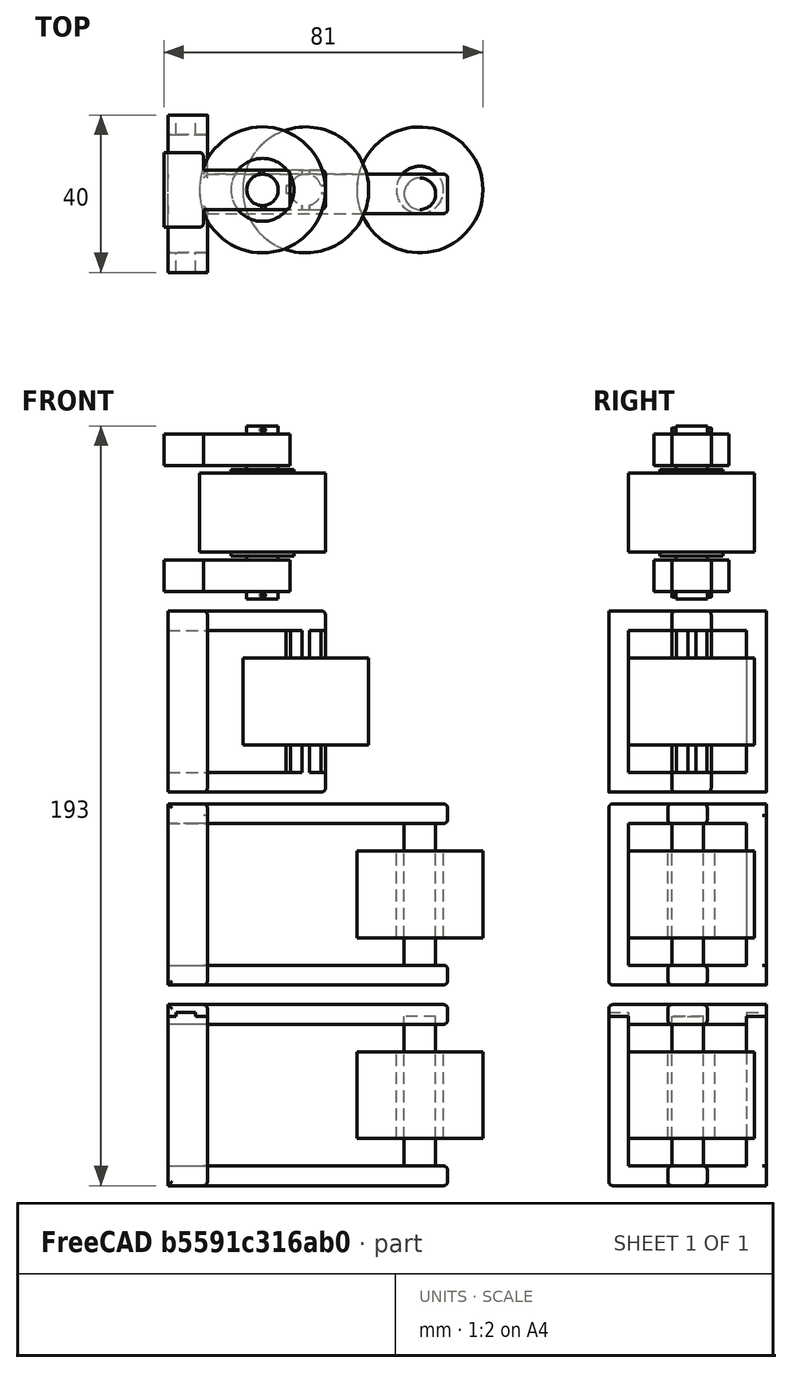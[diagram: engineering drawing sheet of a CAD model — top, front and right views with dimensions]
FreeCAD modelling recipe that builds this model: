
FCSTD DOCUMENT  (FreeCAD 0.17R13541 (Git))
Label: Electrical Tape Holder
License: All rights reserved
LicenseURL: http://en.wikipedia.org/wiki/All_rights_reserved
objects: Part::Box×92, Part::Fillet×65, Part::Cut×41, Part::MultiFuse×41, Part::Cylinder×35
note: 274 computed .brp shape members not serialized (recipe doc carries the construction recipe); baked Part::Feature solids carry a one-line shape summary decoded from their .brp

FEATURE [Part::Cylinder] Cylinder  label="Tape Holder"
  Angle = 360
  AttacherType = Attacher::AttachEngine3D
  Height = 22
  Placement = pos=(110,0,-1) rot=(0,0,1;0rad)
  Radius = 16
FEATURE [Part::Cylinder] Cylinder002  label="Tape Rotation Bar"
  Angle = 360
  AttacherType = Attacher::AttachEngine3D
  Height = 22
  Placement = pos=(110,0,-1) rot=(0,0,1;0rad)
  Radius = 6
FEATURE [Part::Cylinder] Cylinder004  label="Tape Rotation Bar Support Cut Middle"
  Angle = 360
  AttacherType = Attacher::AttachEngine3D
  Height = 40
  Placement = pos=(31,-1,-18) rot=(0,0,1;0rad)
  Radius = 4
FEATURE [Part::Cylinder] Cylinder011  label="Tape Rotation Bar Support Left001"
  Angle = 360
  AttacherType = Attacher::AttachEngine3D
  Height = 40
  Placement = pos=(0,0,-10) rot=(0,0,1;0rad)
  Radius = 4
FEATURE [Part::Cylinder] Cylinder012  label="Tape Rotation Bar Support Right001"
  Angle = 360
  AttacherType = Attacher::AttachEngine3D
  Height = 40
  Placement = pos=(0,0,-10) rot=(0,0,1;0rad)
  Radius = 4
FEATURE [Part::Cylinder] Cylinder013  label="Tape Rotation Bar Support001"
  Angle = 360
  AttacherType = Attacher::AttachEngine3D
  Height = 44
  Placement = pos=(0,0,-12) rot=(0,0,1;0rad)
  Radius = 4
FEATURE [Part::Box] Box007  label="Cube Hinge002"
  AttacherType = Attacher::AttachEngine3D
  Height = 8
  Length = 17
  Placement = pos=(-10,-5,22) rot=(0,0,1;0rad)
  Width = 10
FEATURE [Part::Box] Box008  label="Land Leg 005"
  AttacherType = Attacher::AttachEngine3D
  Height = 8
  Length = 17
  Placement = pos=(-22,-5,22) rot=(0,0,1;0rad)
  Width = 10
FEATURE [Part::Box] Box009  label="Land Leg 006"
  AttacherType = Attacher::AttachEngine3D
  Height = 8
  Length = 19
  Placement = pos=(-15,-9.5,22) rot=(0,0,1;1.5708rad)
  Width = 10
FEATURE [Part::Box] Box010  label="Land Leg 007"
  AttacherType = Attacher::AttachEngine3D
  Height = 8
  Length = 17
  Placement = pos=(-22,-5,22) rot=(0,0,1;0rad)
  Width = 10
FEATURE [Part::Cylinder] Cylinder014  label="Tape Rotation Bar Support Cut Middle001"
  Angle = 360
  AttacherType = Attacher::AttachEngine3D
  Height = 40
  Placement = pos=(0,0,-10) rot=(0,0,1;0rad)
  Radius = 4
FEATURE [Part::Cylinder] Cylinder015  label="Tape Holder001"
  Angle = 360
  AttacherType = Attacher::AttachEngine3D
  Height = 20
  Radius = 16
FEATURE [Part::Cylinder] Cylinder016  label="Tape Rotation Bar001"
  Angle = 360
  AttacherType = Attacher::AttachEngine3D
  Height = 22
  Placement = pos=(0,0,-1) rot=(0,0,1;0rad)
  Radius = 8
FEATURE [Part::Cut] Cut011  label="Middle Support001"
  Base = -> Cylinder016
  Tool = -> Cylinder014
FEATURE [Part::Cylinder] Cylinder017  label="Tape Rotation Hole001"
  Angle = 360
  AttacherType = Attacher::AttachEngine3D
  Height = 22
  Placement = pos=(0,0,-1) rot=(0,0,1;0rad)
  Radius = 8
FEATURE [Part::Cut] Cut009
  Base = -> Cylinder015
  Tool = -> Cylinder017
FEATURE [Part::Box] Box011  label="Land Leg 008"
  AttacherType = Attacher::AttachEngine3D
  Height = 8
  Length = 19
  Placement = pos=(-15,-9.5,22) rot=(0,0,1;1.5708rad)
  Width = 10
FEATURE [Part::MultiFuse] Fusion002
  Shapes = -> [Box007,Box010,Box011]
FEATURE [Part::Cut] Cut010  label="Left Support001"
  Base = -> Fusion002
  Tool = -> Cylinder011
FEATURE [Part::Fillet] Fillet008
  Base = -> Cut010
  Edges = 2 edges r=1: [Edge1,Edge3]
FEATURE [Part::Fillet] Fillet005
  Base = -> Fillet008
  Edges = 2 edges r=1: [Edge45,Edge49]
FEATURE [Part::Box] Box012  label="Cube Hinge003"
  AttacherType = Attacher::AttachEngine3D
  Height = 8
  Length = 17
  Placement = pos=(-10,-5,22) rot=(0,0,1;0rad)
  Width = 10
FEATURE [Part::Cylinder] Cylinder018  label="Lock In Support004"
  Angle = 360
  AttacherType = Attacher::AttachEngine3D
  Height = 10
  Placement = pos=(0.26168,-4.99315,-11) rot=(0.587166,-0.5572,-0.587166;4.1583rad)
  Radius = 0.5
FEATURE [Part::Cylinder] Cylinder019  label="Lock In Support005"
  Angle = 360
  AttacherType = Attacher::AttachEngine3D
  Height = 10
  Placement = pos=(0.26168,-4.99315,31) rot=(0.587166,-0.5572,-0.587166;4.1583rad)
  Radius = 0.5
FEATURE [Part::Cut] Cut006
  Base = -> Cylinder013
  Tool = -> Cylinder019
FEATURE [Part::Cut] Cut007
  Base = -> Cut006
  Tool = -> Cylinder018
FEATURE [Part::Cylinder] Cylinder020  label="Lock In Support006"
  Angle = 360
  AttacherType = Attacher::AttachEngine3D
  Height = 10
  Placement = pos=(0.26168,-4.99315,31) rot=(0.587166,-0.5572,-0.587166;4.1583rad)
  Radius = 0.5
FEATURE [Part::Cylinder] Cylinder021  label="Lock In Support007"
  Angle = 360
  AttacherType = Attacher::AttachEngine3D
  Height = 10
  Placement = pos=(0.26168,-4.99315,-11) rot=(0.587166,-0.5572,-0.587166;4.1583rad)
  Radius = 0.5
FEATURE [Part::MultiFuse] Fusion003
  Placement = pos=(0,0,-32) rot=(0,0,1;0rad)
  Shapes = -> [Box012,Box008,Box009]
FEATURE [Part::Cut] Cut008  label="Right Support001"
  Base = -> Fusion003
  Tool = -> Cylinder012
FEATURE [Part::Fillet] Fillet006
  Base = -> Cut008
  Edges = 2 edges r=1: [Edge1,Edge3]
FEATURE [Part::Fillet] Fillet009
  Base = -> Fillet006
  Edges = 1 edges r=1: [Edge49]
FEATURE [Part::Fillet] Fillet007
  Base = -> Fillet009
  Edges = 1 edges r=1: [Edge28]
FEATURE [Part::Box] Box020  label="Left Leg Support"
  AttacherType = Attacher::AttachEngine3D
  Height = 71
  Length = 5
  Placement = pos=(-35,-6,24) rot=(0,1,0;1.5708rad)
  Width = 10
FEATURE [Part::Box] Box030  label="Right Leg Support"
  AttacherType = Attacher::AttachEngine3D
  Height = 71
  Length = 5
  Placement = pos=(-35,-6,-17) rot=(0,1,0;1.5708rad)
  Width = 10
FEATURE [Part::Box] Box031  label="Cube011"
  AttacherType = Attacher::AttachEngine3D
  Height = 40
  Length = 10
  Placement = pos=(-25,-21,19) rot=(0,0.707107,0.707107;3.14159rad)
  Width = 5
FEATURE [Part::Box] Box043  label="Cube021"
  AttacherType = Attacher::AttachEngine3D
  Height = 40
  Length = 10
  Placement = pos=(-25,-21,-33) rot=(0,1,0;3.14159rad)
  Width = 5
FEATURE [Part::Box] Box055  label="Cube031"
  AttacherType = Attacher::AttachEngine3D
  Height = 42
  Length = 5
  Placement = pos=(-28,-21,-32) rot=(0,1,0;3.14159rad)
  Width = 5
FEATURE [Part::Box] Box056  label="Cube032"
  AttacherType = Attacher::AttachEngine3D
  Height = 40
  Length = 10
  Placement = pos=(-25,-21,21) rot=(0,1,0;3.14159rad)
  Width = 5
FEATURE [Part::Cut] Cut024
  Base = -> Box031
  Tool = -> Box056
FEATURE [Part::Box] Box058  label="Cube034"
  AttacherType = Attacher::AttachEngine3D
  Height = 40
  Length = 10
  Placement = pos=(-25,14,21) rot=(0,1,0;3.14159rad)
  Width = 5
FEATURE [Part::Cut] Cut026
  Base = -> Cut024
  Tool = -> Box058
FEATURE [Part::Fillet] Fillet014
  Base = -> Cut026
  Edges = 1 edges r=1: [Edge5]
FEATURE [Part::MultiFuse] Fusion004  label="Example Model"
  Placement = pos=(0,0,94) rot=(0,0,1;0rad)
  Shapes = -> [Cut007,Cut009,Cut011,Fillet005,Fillet007,Cylinder020,Cylinder021]
FEATURE [Part::Cylinder] Cylinder027  label="Tape Rotation Bar002"
  Angle = 360
  AttacherType = Attacher::AttachEngine3D
  Height = 22
  Placement = pos=(0,0,-1) rot=(0,0,1;0rad)
  Radius = 8
FEATURE [Part::Box] Box059  label="Cube035"
  AttacherType = Attacher::AttachEngine3D
  Height = 40
  Length = 10
  Placement = pos=(-25,-21,19) rot=(0,0.707107,0.707107;3.14159rad)
  Width = 5
FEATURE [Part::Cylinder] Cylinder028  label="Tape Holder002"
  Angle = 360
  AttacherType = Attacher::AttachEngine3D
  Height = 22
  Placement = pos=(0,0,-1) rot=(0,0,1;0rad)
  Radius = 16
FEATURE [Part::Cylinder] Cylinder029  label="Tape Rotation Bar Support002"
  Angle = 360
  AttacherType = Attacher::AttachEngine3D
  Height = 44
  Placement = pos=(0,0,-12) rot=(0,0,1;0rad)
  Radius = 4
FEATURE [Part::Box] Box060  label="Cube036"
  AttacherType = Attacher::AttachEngine3D
  Height = 40
  Length = 10
  Placement = pos=(-25,14,21) rot=(0,1,0;3.14159rad)
  Width = 5
FEATURE [Part::Cylinder] Cylinder030  label="Tape Rotation Bar Support Cut Middle002"
  Angle = 360
  AttacherType = Attacher::AttachEngine3D
  Height = 40
  Placement = pos=(0,0,-10) rot=(0,0,1;0rad)
  Radius = 4
FEATURE [Part::Cut] Cut032  label="Middle Support002"
  Base = -> Cylinder027
  Tool = -> Cylinder030
FEATURE [Part::Cylinder] Cylinder031  label="Tape Rotation Bar Support Right007"
  Angle = 360
  AttacherType = Attacher::AttachEngine3D
  Height = 40
  Placement = pos=(0,0,-74) rot=(0,0,1;0rad)
  Radius = 4
FEATURE [Part::Cylinder] Cylinder032  label="Lock In Support008"
  Angle = 360
  AttacherType = Attacher::AttachEngine3D
  Height = 10
  Placement = pos=(0.26168,-4.99315,31) rot=(0.587166,-0.5572,-0.587166;4.1583rad)
  Radius = 0.5
FEATURE [Part::Cut] Cut033
  Base = -> Cylinder029
  Tool = -> Cylinder032
FEATURE [Part::Cylinder] Cylinder033  label="Lock In Support009"
  Angle = 360
  AttacherType = Attacher::AttachEngine3D
  Height = 10
  Placement = pos=(0.26168,-4.99315,-11) rot=(0.587166,-0.5572,-0.587166;4.1583rad)
  Radius = 0.5
FEATURE [Part::Cut] Cut034
  Base = -> Cut033
  Tool = -> Cylinder033
FEATURE [Part::Cylinder] Cylinder034  label="Tape Rotation Bar Support Right008"
  Angle = 360
  AttacherType = Attacher::AttachEngine3D
  Height = 40
  Placement = pos=(0,0,-74) rot=(0,0,1;0rad)
  Radius = 4
FEATURE [Part::Box] Box061  label="Cube037"
  AttacherType = Attacher::AttachEngine3D
  Height = 5
  Length = 5
  Placement = pos=(-3,4,19) rot=(0,0,1;0rad)
  Width = 5
FEATURE [Part::Cut] Cut036  label="Rotation Lock002"
  Base = -> Cut032
  Placement = pos=(0,0,-64) rot=(0,0,1;0rad)
  Tool = -> Cut034
FEATURE [Part::Box] Box062  label="Cube038"
  AttacherType = Attacher::AttachEngine3D
  Height = 5
  Length = 5
  Placement = pos=(-3,4,19) rot=(0,0,1;0rad)
  Width = 5
FEATURE [Part::Box] Box063  label="Cube039"
  AttacherType = Attacher::AttachEngine3D
  Height = 5
  Length = 5
  Placement = pos=(-9,-2,19) rot=(0,0,1;0rad)
  Width = 5
FEATURE [Part::Box] Box064  label="Cube040"
  AttacherType = Attacher::AttachEngine3D
  Height = 5
  Length = 5
  Placement = pos=(-3,-9,19) rot=(0,0,1;0rad)
  Width = 5
FEATURE [Part::Box] Box065  label="Cube041"
  AttacherType = Attacher::AttachEngine3D
  Height = 5
  Length = 5
  Placement = pos=(4,-2,19) rot=(0,0,1;0rad)
  Width = 5
FEATURE [Part::Box] Box066  label="Cube042"
  AttacherType = Attacher::AttachEngine3D
  Height = 5
  Length = 5
  Placement = pos=(-3,-9,19) rot=(0,0,1;0rad)
  Width = 5
FEATURE [Part::Box] Box067  label="Cube043"
  AttacherType = Attacher::AttachEngine3D
  Height = 5
  Length = 5
  Placement = pos=(-9,-2,19) rot=(0,0,1;0rad)
  Width = 5
FEATURE [Part::Box] Box068  label="Cube044"
  AttacherType = Attacher::AttachEngine3D
  Height = 40
  Length = 5
  Placement = pos=(-35,-5,-17) rot=(0,1,0;1.5708rad)
  Width = 10
FEATURE [Part::MultiFuse] Fusion033
  Placement = pos=(0,0,-41) rot=(0,0,1;0rad)
  Shapes = -> [Box064,Box065,Box063,Box062]
FEATURE [Part::Box] Box069  label="Middle Lock In Bar Cross 013"
  AttacherType = Attacher::AttachEngine3D
  Height = 40
  Length = 10
  Placement = pos=(5.03528,1.1363,-74) rot=(0,0,1;3.14159rad)
  Width = 2
FEATURE [Part::Cylinder] Cylinder035  label="Tape Rotation Bar Support Right009"
  Angle = 360
  AttacherType = Attacher::AttachEngine3D
  Height = 40
  Placement = pos=(0,0,-74) rot=(0,0,1;0rad)
  Radius = 4
FEATURE [Part::Box] Box070  label="Middle Lock In Bar Cross 014"
  AttacherType = Attacher::AttachEngine3D
  Height = 19
  Length = 10
  Placement = pos=(5.03528,1.1363,-65) rot=(0,0,1;3.14159rad)
  Width = 2
FEATURE [Part::Box] Box071  label="Middle Lock In Bar Cross 015"
  AttacherType = Attacher::AttachEngine3D
  Height = 40
  Length = 10
  Placement = pos=(5.03528,1.1363,-74) rot=(0,0,1;3.14159rad)
  Width = 2
FEATURE [Part::Box] Box072  label="Middle Lock In Bar Cross 016"
  AttacherType = Attacher::AttachEngine3D
  Height = 19
  Length = 10
  Placement = pos=(-1,5,-65) rot=(0,0,-1;1.5708rad)
  Width = 2
FEATURE [Part::MultiFuse] Fusion024  label="Rotation Lock Bar Cutout001"
  Shapes = -> [Cylinder035,Box072,Box070]
FEATURE [Part::Cut] Cut044  label="Rotation Lock003"
  Base = -> Cut036
  Tool = -> Fusion024
FEATURE [Part::Cylinder] Cylinder036  label="Tape Rotation Bar Support Right010"
  Angle = 360
  AttacherType = Attacher::AttachEngine3D
  Height = 40
  Placement = pos=(0,0,-74) rot=(0,0,1;0rad)
  Radius = 4
FEATURE [Part::Box] Box073  label="Middle Lock In Bar Cross 017"
  AttacherType = Attacher::AttachEngine3D
  Height = 40
  Length = 10
  Placement = pos=(-1,5,-74) rot=(0,0,-1;1.5708rad)
  Width = 2
FEATURE [Part::MultiFuse] Fusion032  label="Rotation Jock005"
  Placement = pos=(0,0,55) rot=(0,0,1;0rad)
  Shapes = -> [Cylinder034,Box073,Box069]
FEATURE [Part::Box] Box074  label="Middle Lock In Bar Cross 018"
  AttacherType = Attacher::AttachEngine3D
  Height = 40
  Length = 10
  Placement = pos=(-1,5,-74) rot=(0,0,-1;1.5708rad)
  Width = 2
FEATURE [Part::MultiFuse] Fusion025  label="Rotion Lock Bar002"
  Shapes = -> [Cylinder036,Box074,Box071]
FEATURE [Part::Cut] Cut039  label="Rotation Gear002"
  Base = -> Cut044
  Placement = pos=(0,0,64) rot=(0,0,1;0rad)
  Tool = -> Fusion025
FEATURE [Part::MultiFuse] Fusion026  label="Rotation Gear003"
  Placement = pos=(0,0,-3) rot=(0,0,1;0rad)
  Shapes = -> [Cylinder028,Cut039]
FEATURE [Part::Cylinder] Cylinder037  label="Tape Rotation Bar Support Right011"
  Angle = 360
  AttacherType = Attacher::AttachEngine3D
  Height = 40
  Placement = pos=(0,0,-74) rot=(0,0,1;0rad)
  Radius = 4
FEATURE [Part::Box] Box075  label="Cube045"
  AttacherType = Attacher::AttachEngine3D
  Height = 5
  Length = 5
  Placement = pos=(-3,4,19) rot=(0,0,1;0rad)
  Width = 5
FEATURE [Part::Box] Box076  label="Cube046"
  AttacherType = Attacher::AttachEngine3D
  Height = 5
  Length = 5
  Placement = pos=(-3,-9,19) rot=(0,0,1;0rad)
  Width = 5
FEATURE [Part::Box] Box077  label="Cube047"
  AttacherType = Attacher::AttachEngine3D
  Height = 5
  Length = 5
  Placement = pos=(4,-2,19) rot=(0,0,1;0rad)
  Width = 5
FEATURE [Part::MultiFuse] Fusion031
  Shapes = -> [Box076,Box077,Box067,Box075]
FEATURE [Part::Cut] Cut038
  Base = -> Fusion032
  Tool = -> Fusion031
FEATURE [Part::Cut] Cut043
  Base = -> Cut038
  Tool = -> Fusion033
FEATURE [Part::Box] Box078  label="Cube048"
  AttacherType = Attacher::AttachEngine3D
  Height = 40
  Length = 5
  Placement = pos=(-35,-5,24) rot=(0,1,0;1.5708rad)
  Width = 10
FEATURE [Part::Box] Box079  label="Cube049"
  AttacherType = Attacher::AttachEngine3D
  Height = 40
  Length = 10
  Placement = pos=(-25,-21,-22) rot=(0,0.707107,0.707107;3.14159rad)
  Width = 5
FEATURE [Part::Box] Box080  label="Middle Lock In Bar Cross 019"
  AttacherType = Attacher::AttachEngine3D
  Height = 40
  Length = 10
  Placement = pos=(-1,5,-74) rot=(0,0,-1;1.5708rad)
  Width = 2
FEATURE [Part::Box] Box081  label="Middle Lock In Bar Cross 020"
  AttacherType = Attacher::AttachEngine3D
  Height = 40
  Length = 10
  Placement = pos=(5.03528,1.1363,-74) rot=(0,0,1;3.14159rad)
  Width = 2
FEATURE [Part::MultiFuse] Fusion030  label="Rotation Jock Cut001"
  Placement = pos=(0,0,61) rot=(0,0,1;0rad)
  Shapes = -> [Cylinder037,Box080,Box081]
FEATURE [Part::Cut] Cut037  label="Middle Drive Wheel001"
  Base = -> Fusion026
  Placement = pos=(0,0,-6) rot=(0,0,1;0rad)
  Tool = -> Fusion030
FEATURE [Part::Box] Box082  label="Cube050"
  AttacherType = Attacher::AttachEngine3D
  Height = 5
  Length = 5
  Placement = pos=(-9,-2,19) rot=(0,0,1;0rad)
  Width = 5
FEATURE [Part::Box] Box083  label="Cube051"
  AttacherType = Attacher::AttachEngine3D
  Height = 5
  Length = 5
  Placement = pos=(-9,-2,19) rot=(0,0,1;0rad)
  Width = 5
FEATURE [Part::Box] Box084  label="Cube052"
  AttacherType = Attacher::AttachEngine3D
  Height = 5
  Length = 5
  Placement = pos=(-3,4,19) rot=(0,0,1;0rad)
  Width = 5
FEATURE [Part::Box] Box085  label="Cube053"
  AttacherType = Attacher::AttachEngine3D
  Height = 5
  Length = 5
  Placement = pos=(-9,-2,19) rot=(0,0,1;0rad)
  Width = 5
FEATURE [Part::Box] Box086  label="Cube054"
  AttacherType = Attacher::AttachEngine3D
  Height = 5
  Length = 5
  Placement = pos=(-3,4,19) rot=(0,0,1;0rad)
  Width = 5
FEATURE [Part::Cylinder] Cylinder038  label="Tape Rotation Bar Support Right012"
  Angle = 360
  AttacherType = Attacher::AttachEngine3D
  Height = 40
  Placement = pos=(0,0,-74) rot=(0,0,1;0rad)
  Radius = 4
FEATURE [Part::Box] Box087  label="Cube055"
  AttacherType = Attacher::AttachEngine3D
  Height = 5
  Length = 5
  Placement = pos=(-3,-9,19) rot=(0,0,1;0rad)
  Width = 5
FEATURE [Part::Box] Box088  label="Cube056"
  AttacherType = Attacher::AttachEngine3D
  Height = 5
  Length = 5
  Placement = pos=(-3,-9,19) rot=(0,0,1;0rad)
  Width = 5
FEATURE [Part::Box] Box089  label="Middle Lock In Bar Cross 021"
  AttacherType = Attacher::AttachEngine3D
  Height = 40
  Length = 10
  Placement = pos=(5.03528,1.1363,-74) rot=(0,0,1;3.14159rad)
  Width = 2
FEATURE [Part::Box] Box090  label="Cube057"
  AttacherType = Attacher::AttachEngine3D
  Height = 5
  Length = 5
  Placement = pos=(4,-2,19) rot=(0,0,1;0rad)
  Width = 5
FEATURE [Part::MultiFuse] Fusion034
  Shapes = -> [Box087,Box090,Box085,Box084]
FEATURE [Part::Box] Box091  label="Back Support Connector001"
  AttacherType = Attacher::AttachEngine3D
  Height = 40
  Length = 10
  Placement = pos=(-25,14,21) rot=(0,1,0;3.14159rad)
  Width = 5
FEATURE [Part::Box] Box092  label="Cube058"
  AttacherType = Attacher::AttachEngine3D
  Height = 5
  Length = 5
  Placement = pos=(4,-2,19) rot=(0,0,1;0rad)
  Width = 5
FEATURE [Part::MultiFuse] Fusion029
  Placement = pos=(0,0,-41) rot=(0,0,1;0rad)
  Shapes = -> [Box088,Box092,Box083,Box086]
FEATURE [Part::Box] Box093  label="Middle Lock In Bar Cross 022"
  AttacherType = Attacher::AttachEngine3D
  Height = 40
  Length = 10
  Placement = pos=(5.03528,1.1363,-74) rot=(0,0,1;3.14159rad)
  Width = 2
FEATURE [Part::Box] Box094  label="Cube059"
  AttacherType = Attacher::AttachEngine3D
  Height = 40
  Length = 10
  Placement = pos=(-25,-21,21) rot=(0,1,0;3.14159rad)
  Width = 5
FEATURE [Part::Cut] Cut027
  Base = -> Box079
  Tool = -> Box094
FEATURE [Part::Box] Box095  label="Cube060"
  AttacherType = Attacher::AttachEngine3D
  Height = 5
  Length = 5
  Placement = pos=(-9,-2,19) rot=(0,0,1;0rad)
  Width = 5
FEATURE [Part::Box] Box096  label="Middle Lock In Bar Cross 023"
  AttacherType = Attacher::AttachEngine3D
  Height = 40
  Length = 10
  Placement = pos=(-1,5,-74) rot=(0,0,-1;1.5708rad)
  Width = 2
FEATURE [Part::MultiFuse] Fusion022  label="Rotation Jock003"
  Placement = pos=(0,0,55) rot=(0,0,1;0rad)
  Shapes = -> [Cylinder038,Box096,Box093]
FEATURE [Part::Box] Box097  label="Cube061"
  AttacherType = Attacher::AttachEngine3D
  Height = 40
  Length = 10
  Placement = pos=(-25,-21,21) rot=(0,1,0;3.14159rad)
  Width = 5
FEATURE [Part::Box] Box098  label="Cube062"
  AttacherType = Attacher::AttachEngine3D
  Height = 40
  Length = 10
  Placement = pos=(-25,-21,21) rot=(0,1,0;3.14159rad)
  Width = 5
FEATURE [Part::Cut] Cut028
  Base = -> Box059
  Tool = -> Box098
FEATURE [Part::Cut] Cut045
  Base = -> Cut028
  Tool = -> Box060
FEATURE [Part::Fillet] Fillet018
  Base = -> Cut045
  Edges = 1 edges r=1: [Edge5]
FEATURE [Part::Box] Box099  label="Cube063"
  AttacherType = Attacher::AttachEngine3D
  Height = 5
  Length = 5
  Placement = pos=(4,-2,19) rot=(0,0,1;0rad)
  Width = 5
FEATURE [Part::Box] Box100  label="Cube064"
  AttacherType = Attacher::AttachEngine3D
  Height = 5
  Length = 5
  Placement = pos=(-3,4,19) rot=(0,0,1;0rad)
  Width = 5
FEATURE [Part::Box] Box101  label="Cube065"
  AttacherType = Attacher::AttachEngine3D
  Height = 5
  Length = 5
  Placement = pos=(-3,-9,19) rot=(0,0,1;0rad)
  Width = 5
FEATURE [Part::MultiFuse] Fusion023
  Shapes = -> [Box101,Box099,Box095,Box100]
FEATURE [Part::Cut] Cut030
  Base = -> Fusion022
  Tool = -> Fusion023
FEATURE [Part::Cut] Cut031
  Base = -> Cut030
  Tool = -> Fusion029
FEATURE [Part::Cut] Cut035
  Base = -> Box078
  Tool = -> Cut031
FEATURE [Part::Fillet] Fillet020
  Base = -> Cut035
  Edges = 2 edges r=1: [Edge8,Edge10]
FEATURE [Part::Fillet] Fillet017
  Base = -> Fillet020
  Edges = 1 edges r=1: [Edge4]
FEATURE [Part::Box] Box102  label="Middle Lock In Bar Cross 024"
  AttacherType = Attacher::AttachEngine3D
  Height = 40
  Length = 10
  Placement = pos=(-1,5,-74) rot=(0,0,-1;1.5708rad)
  Width = 2
FEATURE [Part::MultiFuse] Fusion027  label="Rotation Jock004"
  Placement = pos=(0,0,55) rot=(0,0,1;0rad)
  Shapes = -> [Cylinder031,Box102,Box089]
FEATURE [Part::Cut] Cut040
  Base = -> Fusion027
  Tool = -> Fusion034
FEATURE [Part::Box] Box103  label="Cube066"
  AttacherType = Attacher::AttachEngine3D
  Height = 5
  Length = 5
  Placement = pos=(4,-2,19) rot=(0,0,1;0rad)
  Width = 5
FEATURE [Part::MultiFuse] Fusion028
  Placement = pos=(0,0,-41) rot=(0,0,1;0rad)
  Shapes = -> [Box066,Box103,Box082,Box061]
FEATURE [Part::Cut] Cut042
  Base = -> Cut040
  Tool = -> Fusion028
FEATURE [Part::Cut] Cut029
  Base = -> Box068
  Tool = -> Cut042
FEATURE [Part::Fillet] Fillet016
  Base = -> Cut029
  Edges = 2 edges r=1: [Edge17,Edge42]
FEATURE [Part::Fillet] Fillet015
  Base = -> Fillet016
  Edges = 1 edges r=1: [Edge9]
FEATURE [Part::Box] Box104  label="Cube067"
  AttacherType = Attacher::AttachEngine3D
  Height = 40
  Length = 10
  Placement = pos=(-25,14,21) rot=(0,1,0;3.14159rad)
  Width = 5
FEATURE [Part::Cut] Cut041
  Base = -> Cut027
  Tool = -> Box104
FEATURE [Part::Fillet] Fillet019
  Base = -> Cut041
  Edges = 1 edges r=1: [Edge8]
FEATURE [Part::MultiFuse] Fusion037  label="Left Support002"
  Shapes = -> [Fillet017,Fillet018]
FEATURE [Part::MultiFuse] Fusion038
  Shapes = -> [Fillet019,Fillet015]
FEATURE [Part::MultiFuse] Fusion039  label="Right Support004"
  Shapes = -> [Cut043,Fusion038]
FEATURE [Part::MultiFuse] Fusion040
  Shapes = -> [Fusion039,Box097]
FEATURE [Part::MultiFuse] Fusion035  label="Right Support003"
  Shapes = -> [Fusion040,Box091]
FEATURE [Part::MultiFuse] Fusion036  label="Example Model 2"
  Placement = pos=(11,0,55) rot=(0,0,1;0rad)
  Shapes = -> [Cut037,Fusion037,Fusion035]
FEATURE [Part::Cut] Cut046
  Base = -> Box020
  Tool = -> Cylinder004
FEATURE [Part::Cut] Cut  label="Rotation Wheel"
  Base = -> Cylinder
  Placement = pos=(-70,0,-54) rot=(0,0,1;0rad)
  Tool = -> Cylinder002
FEATURE [Part::Fillet] Fillet
  Base = -> Box043
  Edges = 2 edges r=1: [Edge1,Edge5]
FEATURE [Part::Fillet] Fillet022
  Base = -> Fillet014
  Edges = 2 edges r=1: [Edge4,Edge19]
FEATURE [Part::MultiFuse] Fusion
  Placement = pos=(0,0,54) rot=(0,0,1;0rad)
  Shapes = -> [Fillet,Box055]
FEATURE [Part::Box] Box105  label="Cube068"
  AttacherType = Attacher::AttachEngine3D
  Height = 42
  Length = 5
  Placement = pos=(-28,-21,-32) rot=(0,1,0;3.14159rad)
  Width = 5
FEATURE [Part::Box] Box106  label="Cube069"
  AttacherType = Attacher::AttachEngine3D
  Height = 40
  Length = 10
  Placement = pos=(-25,-21,-33) rot=(0,1,0;3.14159rad)
  Width = 5
FEATURE [Part::Fillet] Fillet023
  Base = -> Box106
  Edges = 2 edges r=1: [Edge1,Edge5]
FEATURE [Part::MultiFuse] Fusion041
  Placement = pos=(0,0,54) rot=(0,0,1;0rad)
  Shapes = -> [Fillet023,Box105]
FEATURE [Part::Box] Box107  label="Cube070"
  AttacherType = Attacher::AttachEngine3D
  Height = 42
  Length = 5
  Placement = pos=(-28,-21,-32) rot=(0,1,0;3.14159rad)
  Width = 5
FEATURE [Part::Box] Box108  label="Cube071"
  AttacherType = Attacher::AttachEngine3D
  Height = 40
  Length = 10
  Placement = pos=(-25,-21,-33) rot=(0,1,0;3.14159rad)
  Width = 5
FEATURE [Part::Fillet] Fillet024
  Base = -> Box108
  Edges = 2 edges r=1: [Edge3,Edge7]
FEATURE [Part::MultiFuse] Fusion042
  Placement = pos=(0,35,54) rot=(0,0,1;0rad)
  Shapes = -> [Fillet024,Box107]
FEATURE [Part::Box] Box109  label="Cube072"
  AttacherType = Attacher::AttachEngine3D
  Height = 42
  Length = 5
  Placement = pos=(-28,-21,-32) rot=(0,1,0;3.14159rad)
  Width = 5
FEATURE [Part::Box] Box110  label="Cube073"
  AttacherType = Attacher::AttachEngine3D
  Height = 40
  Length = 10
  Placement = pos=(-25,-21,-33) rot=(0,1,0;3.14159rad)
  Width = 5
FEATURE [Part::Fillet] Fillet025
  Base = -> Box110
  Edges = 2 edges r=1: [Edge3,Edge7]
FEATURE [Part::MultiFuse] Fusion043
  Placement = pos=(0,35,54) rot=(0,0,1;0rad)
  Shapes = -> [Fillet025,Box109]
FEATURE [Part::Cut] Cut047
  Base = -> Fillet022
  Tool = -> Fusion
FEATURE [Part::Cut] Cut048
  Base = -> Cut047
  Tool = -> Fusion042
FEATURE [Part::Fillet] Fillet027
  Base = -> Cut048
  Edges = 1 edges r=1: [Edge17]
FEATURE [Part::Box] Box032  label="Cube012"
  AttacherType = Attacher::AttachEngine3D
  Height = 40
  Length = 10
  Placement = pos=(-25,-21,-22) rot=(0,0.707107,0.707107;3.14159rad)
  Width = 5
FEATURE [Part::Fillet] Fillet028
  Base = -> Box032
  Edges = 1 edges r=1: [Edge1]
FEATURE [Part::Fillet] Fillet029
  Base = -> Fillet028
  Edges = 1 edges r=1: [Edge8]
FEATURE [Part::Fillet] Fillet030
  Base = -> Fillet029
  Edges = 2 edges r=1: [Edge13,Edge18]
FEATURE [Part::Fillet] Fillet031
  Base = -> Box030
  Edges = 1 edges r=1: [Edge5]
FEATURE [Part::Fillet] Fillet032
  Base = -> Fillet031
  Edges = 1 edges r=1: [Edge3]
FEATURE [Part::Fillet] Fillet033
  Base = -> Cut046
  Edges = 1 edges r=1: [Edge3]
FEATURE [Part::Fillet] Fillet034
  Base = -> Fillet033
  Edges = 1 edges r=1: [Edge3]
FEATURE [Part::Fillet] Fillet035
  Base = -> Fillet034
  Edges = 1 edges r=1: [Edge1]
FEATURE [Part::Fillet] Fillet036
  Base = -> Fillet032
  Edges = 1 edges r=1: [Edge1]
FEATURE [Part::Fillet] Fillet037
  Base = -> Fillet035
  Edges = 1 edges r=1: [Edge21]
FEATURE [Part::Fillet] Fillet038
  Base = -> Fillet036
  Edges = 1 edges r=1: [Edge23]
FEATURE [Part::Cylinder] Cylinder039  label="Tape Rotation Bar Support Right013"
  Angle = 360
  AttacherType = Attacher::AttachEngine3D
  Height = 40
  Placement = pos=(29,-1,-19) rot=(0,0,1;0rad)
  Radius = 4
FEATURE [Part::Cylinder] Cylinder040  label="Tape Rotation Bar Support Right014"
  Angle = 360
  AttacherType = Attacher::AttachEngine3D
  Height = 40
  Placement = pos=(29,-1,-19) rot=(0,0,1;0rad)
  Radius = 4
FEATURE [Part::Cut] Cut049
  Base = -> Fillet037
  Tool = -> Cylinder040
FEATURE [Part::MultiFuse] Fusion044
  Shapes = -> [Fusion041,Fusion043,Fillet030,Fillet038,Cylinder039]
FEATURE [Part::Box] Box111  label="Cube074"
  AttacherType = Attacher::AttachEngine3D
  Height = 42
  Length = 5
  Placement = pos=(-28,-21,-32) rot=(0,1,0;3.14159rad)
  Width = 5
FEATURE [Part::Box] Box112  label="Cube075"
  AttacherType = Attacher::AttachEngine3D
  Height = 42
  Length = 5
  Placement = pos=(-28,-21,-32) rot=(0,1,0;3.14159rad)
  Width = 5
FEATURE [Part::Box] Box113  label="Cube076"
  AttacherType = Attacher::AttachEngine3D
  Height = 40
  Length = 10
  Placement = pos=(-25,-21,-22) rot=(0,0.707107,0.707107;3.14159rad)
  Width = 5
FEATURE [Part::Box] Box114  label="Cube077"
  AttacherType = Attacher::AttachEngine3D
  Height = 40
  Length = 10
  Placement = pos=(-25,-21,-33) rot=(0,1,0;3.14159rad)
  Width = 5
FEATURE [Part::Box] Box115  label="Cube078"
  AttacherType = Attacher::AttachEngine3D
  Height = 40
  Length = 10
  Placement = pos=(-25,-21,-33) rot=(0,1,0;3.14159rad)
  Width = 5
FEATURE [Part::Box] Box116  label="Right Leg Support001"
  AttacherType = Attacher::AttachEngine3D
  Height = 71
  Length = 5
  Placement = pos=(-35,-6,-17) rot=(0,1,0;1.5708rad)
  Width = 10
FEATURE [Part::Cylinder] Cylinder041  label="Tape Rotation Bar Support Right015"
  Angle = 360
  AttacherType = Attacher::AttachEngine3D
  Height = 40
  Placement = pos=(29,-1,-19) rot=(0,0,1;0rad)
  Radius = 4
FEATURE [Part::Fillet] Fillet040
  Base = -> Box115
  Edges = 2 edges r=1: [Edge3,Edge7]
FEATURE [Part::MultiFuse] Fusion046
  Placement = pos=(0,35,54) rot=(0,0,1;0rad)
  Shapes = -> [Fillet040,Box112]
FEATURE [Part::Fillet] Fillet042
  Base = -> Box113
  Edges = 1 edges r=1: [Edge1]
FEATURE [Part::Fillet] Fillet039
  Base = -> Fillet042
  Edges = 1 edges r=1: [Edge8]
FEATURE [Part::Fillet] Fillet043
  Base = -> Fillet039
  Edges = 2 edges r=1: [Edge13,Edge18]
FEATURE [Part::Fillet] Fillet044
  Base = -> Box116
  Edges = 1 edges r=1: [Edge5]
FEATURE [Part::Fillet] Fillet041
  Base = -> Fillet044
  Edges = 1 edges r=1: [Edge3]
FEATURE [Part::Fillet] Fillet045
  Base = -> Box114
  Edges = 2 edges r=1: [Edge1,Edge5]
FEATURE [Part::MultiFuse] Fusion047
  Placement = pos=(0,0,54) rot=(0,0,1;0rad)
  Shapes = -> [Fillet045,Box111]
FEATURE [Part::Fillet] Fillet047
  Base = -> Fillet041
  Edges = 1 edges r=1: [Edge1]
FEATURE [Part::Fillet] Fillet046
  Base = -> Fillet047
  Edges = 1 edges r=1: [Edge23]
FEATURE [Part::MultiFuse] Fusion045  label="Right Leg Support002"
  Placement = pos=(11,0,-45) rot=(0,0,1;0rad)
  Shapes = -> [Fusion047,Fusion046,Fillet043,Fillet046,Cylinder041]
FEATURE [Part::MultiFuse] Fusion048
  Shapes = -> [Fillet027,Cut049]
FEATURE [Part::Cut] Cut050  label="Left Leg Support001"
  Base = -> Fusion048
  Placement = pos=(11,0,-45) rot=(0,0,1;0rad)
  Tool = -> Fusion044
FEATURE [Part::Cylinder] Cylinder042  label="Tape Holder003"
  Angle = 360
  AttacherType = Attacher::AttachEngine3D
  Height = 22
  Placement = pos=(110,0,-1) rot=(0,0,1;0rad)
  Radius = 16
FEATURE [Part::Cylinder] Cylinder043  label="Tape Rotation Bar003"
  Angle = 360
  AttacherType = Attacher::AttachEngine3D
  Height = 22
  Placement = pos=(110,0,-1) rot=(0,0,1;0rad)
  Radius = 6
FEATURE [Part::Cylinder] Cylinder044  label="Tape Rotation Bar Support Cut Middle003"
  Angle = 360
  AttacherType = Attacher::AttachEngine3D
  Height = 40
  Placement = pos=(31,-1,-18) rot=(0,0,1;0rad)
  Radius = 4
FEATURE [Part::Box] Box117  label="Cube079"
  AttacherType = Attacher::AttachEngine3D
  Height = 42
  Length = 5
  Placement = pos=(-28,-21,-32) rot=(0,1,0;3.14159rad)
  Width = 5
FEATURE [Part::Box] Box118  label="Cube080"
  AttacherType = Attacher::AttachEngine3D
  Height = 42
  Length = 5
  Placement = pos=(-28,-21,-32) rot=(0,1,0;3.14159rad)
  Width = 5
FEATURE [Part::Box] Box119  label="Left Leg Support002"
  AttacherType = Attacher::AttachEngine3D
  Height = 71
  Length = 5
  Placement = pos=(-35,-6,24) rot=(0,1,0;1.5708rad)
  Width = 10
FEATURE [Part::Box] Box120  label="Cube081"
  AttacherType = Attacher::AttachEngine3D
  Height = 40
  Length = 10
  Placement = pos=(-25,-21,-22) rot=(0,0.707107,0.707107;3.14159rad)
  Width = 5
FEATURE [Part::Box] Box121  label="Cube082"
  AttacherType = Attacher::AttachEngine3D
  Height = 42
  Length = 5
  Placement = pos=(-28,-21,-32) rot=(0,1,0;3.14159rad)
  Width = 5
FEATURE [Part::Box] Box122  label="Cube083"
  AttacherType = Attacher::AttachEngine3D
  Height = 40
  Length = 10
  Placement = pos=(-25,-21,-33) rot=(0,1,0;3.14159rad)
  Width = 5
FEATURE [Part::Box] Box123  label="Cube084"
  AttacherType = Attacher::AttachEngine3D
  Height = 40
  Length = 10
  Placement = pos=(-25,-21,-33) rot=(0,1,0;3.14159rad)
  Width = 5
FEATURE [Part::Box] Box124  label="Cube085"
  AttacherType = Attacher::AttachEngine3D
  Height = 40
  Length = 10
  Placement = pos=(-25,-21,-33) rot=(0,1,0;3.14159rad)
  Width = 5
FEATURE [Part::Box] Box125  label="Right Leg Support003"
  AttacherType = Attacher::AttachEngine3D
  Height = 71
  Length = 5
  Placement = pos=(-35,-6,-17) rot=(0,1,0;1.5708rad)
  Width = 10
FEATURE [Part::Box] Box126  label="Cube086"
  AttacherType = Attacher::AttachEngine3D
  Height = 40
  Length = 10
  Placement = pos=(-25,-21,19) rot=(0,0.707107,0.707107;3.14159rad)
  Width = 5
FEATURE [Part::Box] Box127  label="Cube087"
  AttacherType = Attacher::AttachEngine3D
  Height = 40
  Length = 10
  Placement = pos=(-25,14,21) rot=(0,1,0;3.14159rad)
  Width = 5
FEATURE [Part::Box] Box128  label="Cube088"
  AttacherType = Attacher::AttachEngine3D
  Height = 42
  Length = 5
  Placement = pos=(-28,-21,-32) rot=(0,1,0;3.14159rad)
  Width = 5
FEATURE [Part::Box] Box129  label="Cube089"
  AttacherType = Attacher::AttachEngine3D
  Height = 40
  Length = 10
  Placement = pos=(-25,-21,-22) rot=(0,0.707107,0.707107;3.14159rad)
  Width = 5
FEATURE [Part::Fillet] Fillet053
  Base = -> Box129
  Edges = 1 edges r=1: [Edge1]
FEATURE [Part::Fillet] Fillet049
  Base = -> Fillet053
  Edges = 1 edges r=1: [Edge8]
FEATURE [Part::Fillet] Fillet048
  Base = -> Fillet049
  Edges = 2 edges r=1: [Edge13,Edge18]
FEATURE [Part::Box] Box130  label="Cube090"
  AttacherType = Attacher::AttachEngine3D
  Height = 40
  Length = 10
  Placement = pos=(-25,-21,-33) rot=(0,1,0;3.14159rad)
  Width = 5
FEATURE [Part::Fillet] Fillet051
  Base = -> Box130
  Edges = 2 edges r=1: [Edge3,Edge7]
FEATURE [Part::Cylinder] Cylinder045  label="Tape Rotation Bar Support Right016"
  Angle = 360
  AttacherType = Attacher::AttachEngine3D
  Height = 40
  Placement = pos=(29,-1,-19) rot=(0,0,1;0rad)
  Radius = 4
FEATURE [Part::Box] Box131  label="Cube091"
  AttacherType = Attacher::AttachEngine3D
  Height = 42
  Length = 5
  Placement = pos=(-28,-21,-32) rot=(0,1,0;3.14159rad)
  Width = 5
FEATURE [Part::Box] Box132  label="Cube092"
  AttacherType = Attacher::AttachEngine3D
  Height = 40
  Length = 10
  Placement = pos=(-25,-21,-33) rot=(0,1,0;3.14159rad)
  Width = 5
FEATURE [Part::Cylinder] Cylinder046  label="Tape Rotation Bar Support Right017"
  Angle = 360
  AttacherType = Attacher::AttachEngine3D
  Height = 40
  Placement = pos=(29,-1,-19) rot=(0,0,1;0rad)
  Radius = 4
FEATURE [Part::Box] Box133  label="Cube093"
  AttacherType = Attacher::AttachEngine3D
  Height = 42
  Length = 5
  Placement = pos=(-28,-21,-32) rot=(0,1,0;3.14159rad)
  Width = 5
FEATURE [Part::MultiFuse] Fusion049
  Placement = pos=(0,35,54) rot=(0,0,1;0rad)
  Shapes = -> [Fillet051,Box133]
FEATURE [Part::Box] Box134  label="Cube094"
  AttacherType = Attacher::AttachEngine3D
  Height = 40
  Length = 10
  Placement = pos=(-25,-21,-33) rot=(0,1,0;3.14159rad)
  Width = 5
FEATURE [Part::Box] Box135  label="Right Leg Support005"
  AttacherType = Attacher::AttachEngine3D
  Height = 71
  Length = 5
  Placement = pos=(-35,-6,-17) rot=(0,1,0;1.5708rad)
  Width = 10
FEATURE [Part::Cylinder] Cylinder047  label="Tape Rotation Bar Support Right018"
  Angle = 360
  AttacherType = Attacher::AttachEngine3D
  Height = 40
  Placement = pos=(29,-1,-19) rot=(0,0,1;0rad)
  Radius = 4
FEATURE [Part::Box] Box136  label="Cube095"
  AttacherType = Attacher::AttachEngine3D
  Height = 40
  Length = 10
  Placement = pos=(-25,-21,21) rot=(0,1,0;3.14159rad)
  Width = 5
FEATURE [Part::Cut] Cut052
  Base = -> Box126
  Tool = -> Box136
FEATURE [Part::Cut] Cut051
  Base = -> Cut052
  Tool = -> Box127
FEATURE [Part::Fillet] Fillet050
  Base = -> Cut051
  Edges = 1 edges r=1: [Edge5]
FEATURE [Part::Cut] Cut054  label="Rotation Wheel001"
  Base = -> Cylinder042
  Placement = pos=(-81,0,-9) rot=(0,0,1;0rad)
  Tool = -> Cylinder043
FEATURE [Part::Cut] Cut058
  Base = -> Box119
  Tool = -> Cylinder044
FEATURE [Part::Fillet] Fillet054
  Base = -> Box132
  Edges = 2 edges r=1: [Edge1,Edge5]
FEATURE [Part::MultiFuse] Fusion057
  Placement = pos=(0,0,54) rot=(0,0,1;0rad)
  Shapes = -> [Fillet054,Box128]
FEATURE [Part::Fillet] Fillet056
  Base = -> Box123
  Edges = 2 edges r=1: [Edge3,Edge7]
FEATURE [Part::MultiFuse] Fusion054
  Placement = pos=(0,35,54) rot=(0,0,1;0rad)
  Shapes = -> [Fillet056,Box118]
FEATURE [Part::Fillet] Fillet058
  Base = -> Cut058
  Edges = 1 edges r=1: [Edge3]
FEATURE [Part::Fillet] Fillet060
  Base = -> Fillet050
  Edges = 2 edges r=1: [Edge4,Edge19]
FEATURE [Part::Cut] Cut056
  Base = -> Fillet060
  Tool = -> Fusion057
FEATURE [Part::Fillet] Fillet061
  Base = -> Box120
  Edges = 1 edges r=1: [Edge1]
FEATURE [Part::Fillet] Fillet055
  Base = -> Fillet061
  Edges = 1 edges r=1: [Edge8]
FEATURE [Part::Fillet] Fillet062
  Base = -> Box124
  Edges = 2 edges r=1: [Edge3,Edge7]
FEATURE [Part::MultiFuse] Fusion056
  Placement = pos=(0,35,54) rot=(0,0,1;0rad)
  Shapes = -> [Fillet062,Box121]
FEATURE [Part::Cut] Cut057
  Base = -> Cut056
  Tool = -> Fusion056
FEATURE [Part::Fillet] Fillet063
  Base = -> Fillet055
  Edges = 2 edges r=1: [Edge13,Edge18]
FEATURE [Part::Fillet] Fillet064
  Base = -> Box125
  Edges = 1 edges r=1: [Edge5]
FEATURE [Part::Fillet] Fillet057
  Base = -> Fillet064
  Edges = 1 edges r=1: [Edge3]
FEATURE [Part::Fillet] Fillet065
  Base = -> Fillet058
  Edges = 1 edges r=1: [Edge3]
FEATURE [Part::Fillet] Fillet059
  Base = -> Fillet065
  Edges = 1 edges r=1: [Edge1]
FEATURE [Part::Fillet] Fillet066
  Base = -> Box122
  Edges = 2 edges r=1: [Edge1,Edge5]
FEATURE [Part::MultiFuse] Fusion058
  Placement = pos=(0,0,54) rot=(0,0,1;0rad)
  Shapes = -> [Fillet066,Box117]
FEATURE [Part::Fillet] Fillet068
  Base = -> Cut057
  Edges = 1 edges r=1: [Edge17]
FEATURE [Part::Fillet] Fillet069
  Base = -> Fillet057
  Edges = 1 edges r=1: [Edge1]
FEATURE [Part::Fillet] Fillet067
  Base = -> Fillet069
  Edges = 1 edges r=1: [Edge23]
FEATURE [Part::MultiFuse] Fusion053
  Shapes = -> [Fusion058,Fusion054,Fillet063,Fillet067,Cylinder045]
FEATURE [Part::Fillet] Fillet070
  Base = -> Fillet059
  Edges = 1 edges r=1: [Edge21]
FEATURE [Part::Cut] Cut053
  Base = -> Fillet070
  Tool = -> Cylinder046
FEATURE [Part::MultiFuse] Fusion055
  Shapes = -> [Fillet068,Cut053]
FEATURE [Part::Cut] Cut055  label="Left Leg Support003"
  Base = -> Fusion055
  Tool = -> Fusion053
FEATURE [Part::Fillet] Fillet072
  Base = -> Box134
  Edges = 2 edges r=1: [Edge1,Edge5]
FEATURE [Part::MultiFuse] Fusion050
  Placement = pos=(0,0,54) rot=(0,0,1;0rad)
  Shapes = -> [Fillet072,Box131]
FEATURE [Part::Fillet] Fillet073
  Base = -> Box135
  Edges = 1 edges r=1: [Edge5]
FEATURE [Part::Fillet] Fillet052
  Base = -> Fillet073
  Edges = 1 edges r=1: [Edge3]
FEATURE [Part::Fillet] Fillet074
  Base = -> Fillet052
  Edges = 1 edges r=1: [Edge1]
FEATURE [Part::Fillet] Fillet071
  Base = -> Fillet074
  Edges = 1 edges r=1: [Edge23]
FEATURE [Part::MultiFuse] Fusion052  label="Right Leg Support004"
  Shapes = -> [Fusion050,Fusion049,Fillet048,Fillet071,Cylinder047]
FEATURE [Part::MultiFuse] Fusion051
  Placement = pos=(11,0,6) rot=(0,0,1;0rad)
  Shapes = -> [Fusion052,Cut055,Cut054]
